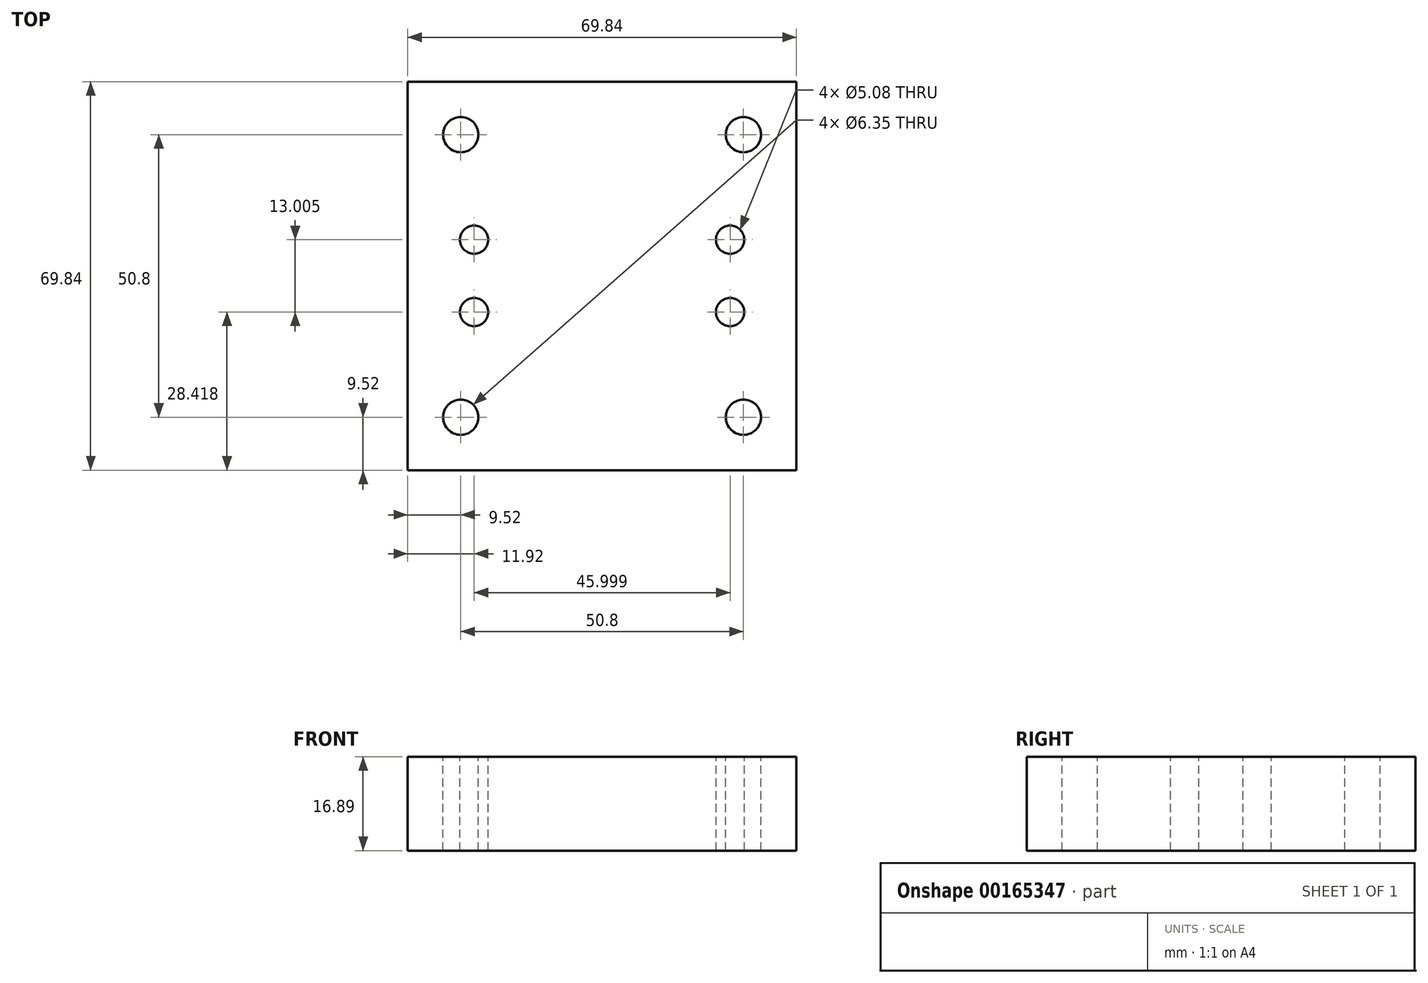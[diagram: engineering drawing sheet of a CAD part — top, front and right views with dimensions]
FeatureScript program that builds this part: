
annotation { "Feature Type Name" : "Feature", "Feature Type Description" : "" }
export const myFeature = defineFeature(function(context is Context, id is Id, definition is map)
    precondition{}
    {
        {
            var Q0;
            Q0=qCreatedBy(makeId("Top.planeOp"),FACE);
            var sketch = newSketch(context, id + "F0", { "sketchPlane" : qUnion([Q0])});
            skLineSegment(sketch, "E0.rect.bottom", {"start": v(34.92, 34.93) * mm, "end": v(-34.93, 34.93) * mm});
            skLineSegment(sketch, "E0.rect.top", {"start": v(34.93, -34.93) * mm, "end": v(-34.92, -34.93) * mm});
            skLineSegment(sketch, "E0.rect.left", {"start": v(34.93, 34.93) * mm, "end": v(34.93, -34.93) * mm});
            skLineSegment(sketch, "E0.rect.right", {"start": v(-34.93, 34.93) * mm, "end": v(-34.92, -34.93) * mm});
            skPoint(sketch, "E0.rect.middle", {"position": v(0, 0) * mm});
            skSolve(sketch);
        }
        {
            var Q0;
            Q0=qSketchRegion(id+"F0",true);
            extrude(context, id + "F1", {"entities" : qUnion([Q0]), "depth" : 16.9 * mm});
        }
        {
            var Q0;
            Q0=makeQuery(id+"F1.opExtrude","CAP_FACE",FACE,{"disambiguationData":[OSD([sQuery(id+"F0.wireOp",EDGE,"E0.rect.bottom"),sQuery(id+"F0.wireOp",EDGE,"E0.rect.top"),sQuery(id+"F0.wireOp",EDGE,"E0.rect.left"),sQuery(id+"F0.wireOp",EDGE,"E0.rect.right")])],"isStart":false});
            var sketch = newSketch(context, id + "F2", { "sketchPlane" : qUnion([Q0])});
            skLineSegment(sketch, "E1.rect.bottom", {"start": v(-23, 6.5) * mm, "end": v(23, 6.5) * mm, "construction": true});
            skLineSegment(sketch, "E1.rect.top", {"start": v(-23, -6.5) * mm, "end": v(23, -6.5) * mm, "construction": true});
            skLineSegment(sketch, "E1.rect.left", {"start": v(-23, 6.5) * mm, "end": v(-23, -6.5) * mm, "construction": true});
            skLineSegment(sketch, "E1.rect.right", {"start": v(23, 6.5) * mm, "end": v(23, -6.5) * mm, "construction": true});
            skPoint(sketch, "E1.rect.middle", {"position": v(0, 0) * mm});
            skCircle(sketch, "E2", {"center": v(-23, 6.5) * mm, "radius": 2.54 * mm});
            skCircle(sketch, "E3", {"center": v(23, 6.5) * mm, "radius": 2.54 * mm});
            skCircle(sketch, "E4", {"center": v(23, -6.5) * mm, "radius": 2.54 * mm});
            skCircle(sketch, "E5", {"center": v(-23, -6.5) * mm, "radius": 2.54 * mm});
            skSolve(sketch);
        }
        {
            var Q0;
            Q0=qSketchRegion(id+"F2",true);
            extrude(context, id + "F3", {"entities" : qUnion([Q0]), "operationType" : NewBodyOperationType.REMOVE, "endBound" : BoundingType.THROUGH_ALL, "oppositeDirection" : true, "depth" : 25.4 * mm});
        }
        {
            var Q0;
            Q0=makeQuery(id+"F1.opExtrude","CAP_FACE",FACE,{"disambiguationData":[OSD([sQuery(id+"F0.wireOp",EDGE,"E0.rect.bottom"),sQuery(id+"F0.wireOp",EDGE,"E0.rect.top"),sQuery(id+"F0.wireOp",EDGE,"E0.rect.left"),sQuery(id+"F0.wireOp",EDGE,"E0.rect.right")])],"isStart":false});
            var sketch = newSketch(context, id + "F4", { "sketchPlane" : qUnion([Q0])});
            skLineSegment(sketch, "E6.bottom", {"start": v(25.4, -25.4) * mm, "end": v(-25.4, -25.4) * mm, "construction": true});
            skLineSegment(sketch, "E6.top", {"start": v(25.4, 25.4) * mm, "end": v(-25.4, 25.4) * mm, "construction": true});
            skLineSegment(sketch, "E6.left", {"start": v(25.4, -25.4) * mm, "end": v(25.4, 25.4) * mm, "construction": true});
            skLineSegment(sketch, "E6.right", {"start": v(-25.4, -25.4) * mm, "end": v(-25.4, 25.4) * mm, "construction": true});
            skPoint(sketch, "E6.middle", {"position": v(0, 0) * mm});
            skCircle(sketch, "E7", {"center": v(-25.4, 25.4) * mm, "radius": 3.18 * mm});
            skCircle(sketch, "E8", {"center": v(25.4, 25.4) * mm, "radius": 3.18 * mm});
            skCircle(sketch, "E9", {"center": v(-25.4, -25.4) * mm, "radius": 3.18 * mm});
            skCircle(sketch, "E10", {"center": v(25.4, -25.4) * mm, "radius": 3.18 * mm});
            skSolve(sketch);
        }
        {
            var Q0;
            Q0=qSketchRegion(id+"F4",true);
            extrude(context, id + "F5", {"entities" : qUnion([Q0]), "operationType" : NewBodyOperationType.REMOVE, "endBound" : BoundingType.THROUGH_ALL, "oppositeDirection" : true, "depth" : 25.4 * mm});
        }
    });
